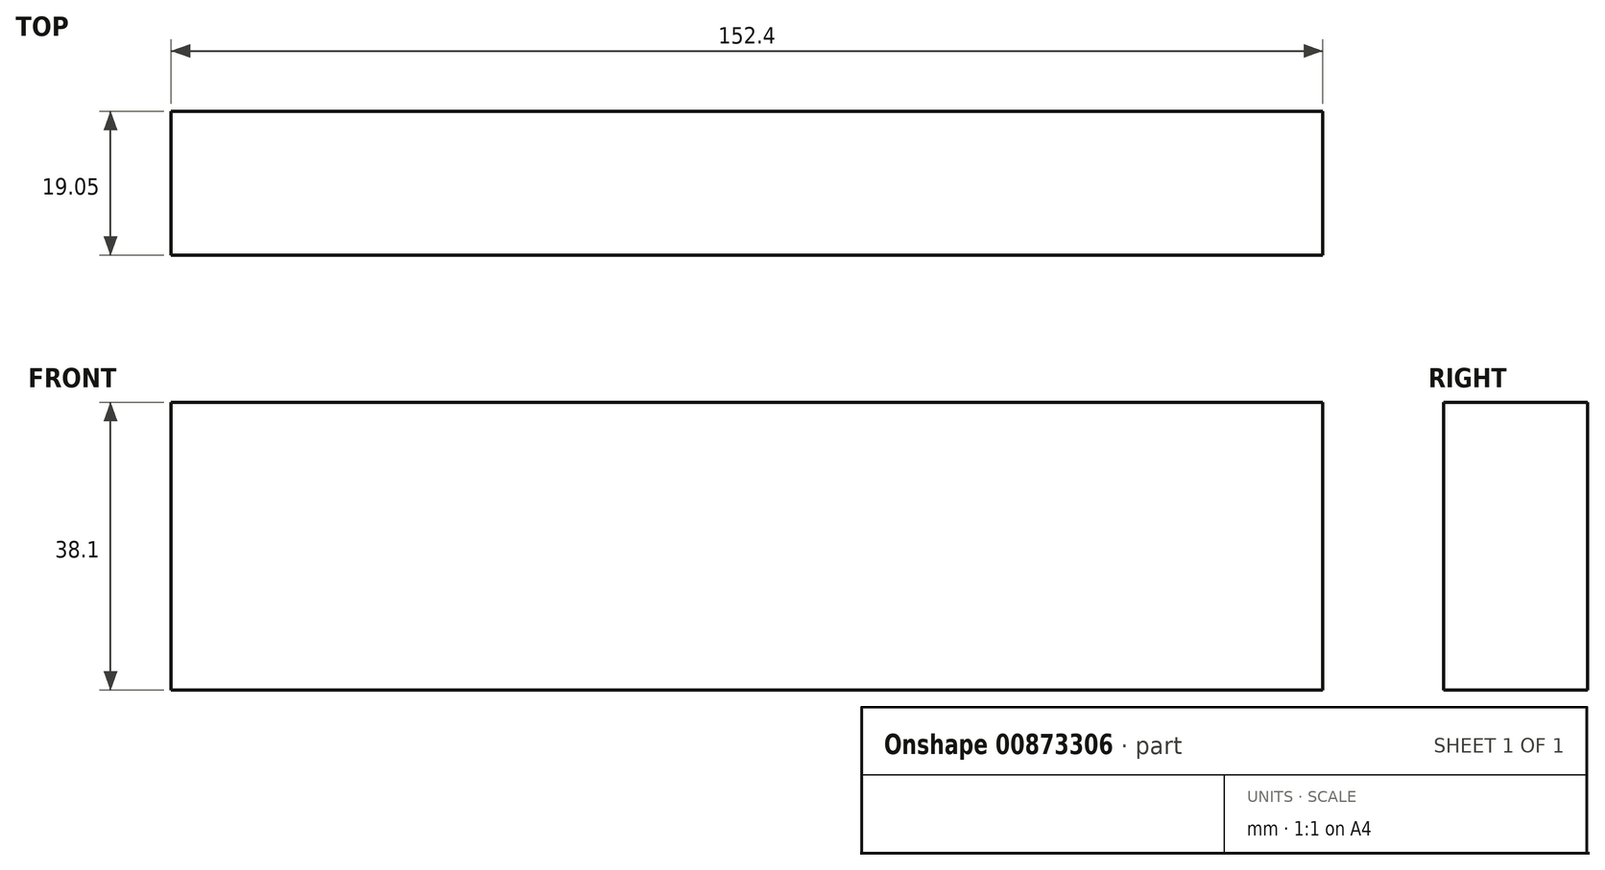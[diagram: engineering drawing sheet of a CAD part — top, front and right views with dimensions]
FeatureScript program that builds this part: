
annotation { "Feature Type Name" : "Feature", "Feature Type Description" : "" }
export const myFeature = defineFeature(function(context is Context, id is Id, definition is map)
    precondition{}
    {
        {
            var Q0;
            Q0=qCreatedBy(makeId("Front.planeOp"),FACE);
            var sketch = newSketch(context, id + "F0", { "sketchPlane" : qUnion([Q0])});
            skLineSegment(sketch, "E0.bottom", {"start": v(0, 0) * mm, "end": v(-152.4, 0) * mm});
            skLineSegment(sketch, "E0.top", {"start": v(0, 38.1) * mm, "end": v(-152.4, 38.1) * mm});
            skLineSegment(sketch, "E0.left", {"start": v(0, 0) * mm, "end": v(0, 38.1) * mm});
            skLineSegment(sketch, "E0.right", {"start": v(-152.4, 0) * mm, "end": v(-152.4, 38.1) * mm});
            skSolve(sketch);
        }
        {
            var Q0;
            Q0=qSketchRegion(id+"F0",true);
            extrude(context, id + "F1", {"entities" : qUnion([Q0]), "depth" : 19.05 * mm, "offsetDistance" : 25.4 * mm});
        }
    });
